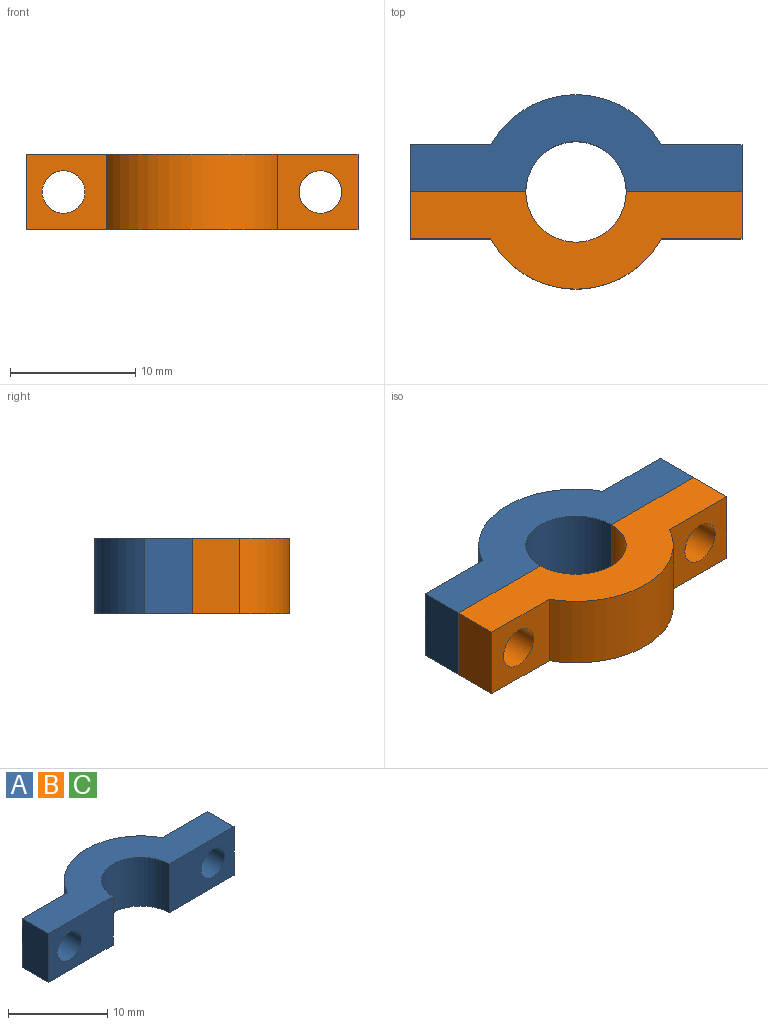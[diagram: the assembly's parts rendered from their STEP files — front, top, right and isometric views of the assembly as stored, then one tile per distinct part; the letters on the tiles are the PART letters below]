
ASSEMBLY  parts=3 mates=1
PART A: 12 faces, bbox 26.5x7.8x6 mm
  f0: plane 6.45x6mm, normal (0,1,0), area 29.6mm2, adj f1,f7,f8,f9,f11
  f1: plane 6x3.75mm, normal (-1,0,0), area 22.5mm2, adj f0,f2,f8,f9
  f2: plane 9.23x6mm, normal (0,-1,0), area 46.3mm2, adj f1,f3,f8,f9,f11
  f3: cylinder r=4mm len=8mm, axis (0,0,-1), area 75.4mm2, adj f2,f4,f8,f9
  f4: plane 9.23x6mm, normal (0,-1,0), area 46.3mm2, adj f3,f5,f8,f9,f10
  f5: plane 6x3.75mm, normal (1,0,0), area 22.5mm2, adj f4,f6,f8,f9
  f6: plane 6.45x6mm, normal (0,1,0), area 29.6mm2, adj f5,f7,f8,f9,f10
  f7: cylinder r=7.75mm len=13.56mm, axis (0,0,-1), area 99.1mm2, adj f0,f6,f8,f9
  f8: plane 26.46x7.75mm, normal (0,0,1), area 112.7mm2, adj f0,f1,f2,f3,f4,f5,f6,f7
  f9: plane 26.46x7.75mm, normal (0,0,-1), area 112.7mm2, adj f0,f1,f2,f3,f4,f5,f6,f7
  f10: cylinder r=1.7mm len=3.75mm, axis (0,1,0), area 40.1mm2, adj f4,f6
  f11: cylinder r=1.7mm len=3.75mm, axis (0,1,0), area 40.1mm2, adj f0,f2
PART B: same geometry as A
PART C: same geometry as A
PLACE A t=(-1.75,-1.45,3.09)mm
PLACE B rot(axis=(1,0,0),180deg) t=(-1.75,-1.45,9.09)mm
PLACE C t=(-1.75,-1.45,3.09)mm
MATE fastened B.f2 <-> A.f2  axis (0,1,0) through (-10.05,-1.45,6.09)mm
